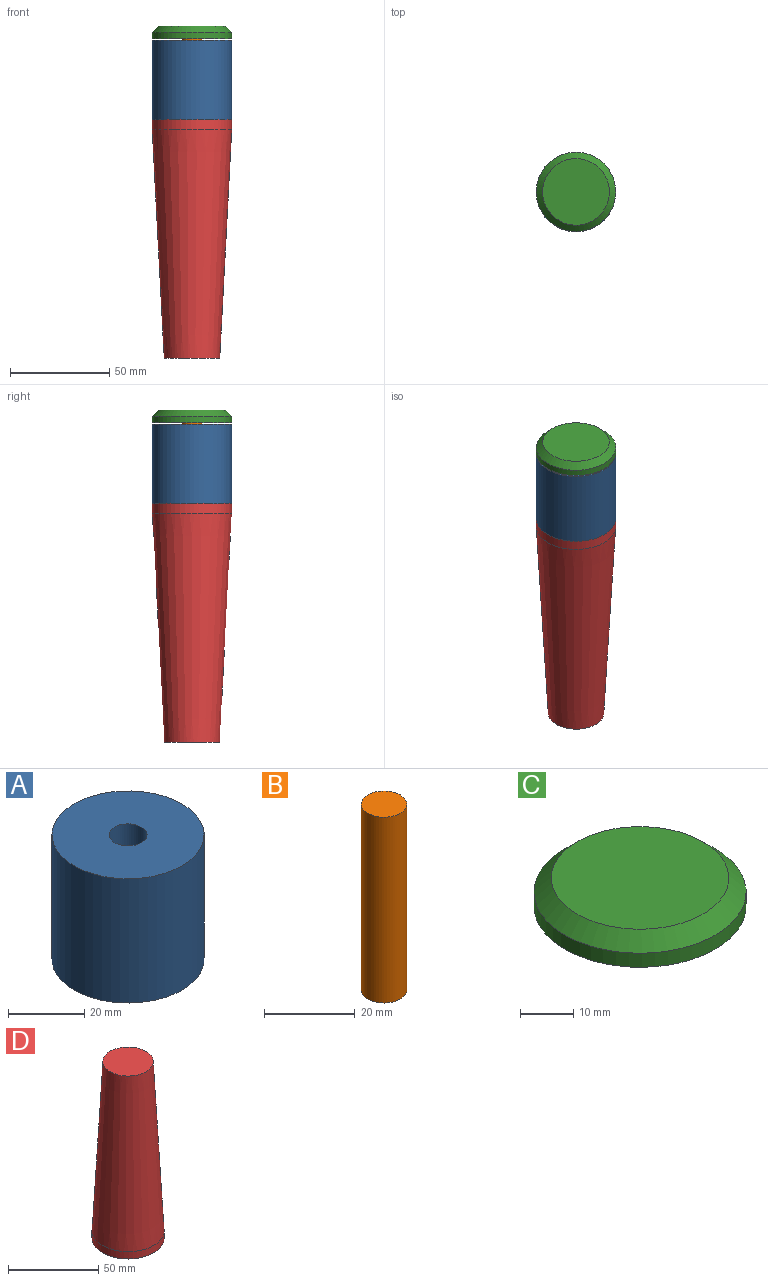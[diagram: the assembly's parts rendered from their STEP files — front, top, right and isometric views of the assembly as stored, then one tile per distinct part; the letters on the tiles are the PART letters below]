
ASSEMBLY  parts=4 mates=3
PART A: 4 faces, bbox 40x40x40 mm
  f0: cylinder r=5mm len=40mm, axis (0,0,-1), area 1256.6mm2, adj f2,f3
  f1: cylinder r=20mm len=40mm, axis (0,0,-1), area 5026.5mm2, adj f2,f3
  f2: plane 40x40mm, normal (0,0,1), area 1178.1mm2, adj f0,f1
  f3: plane 40x40mm, normal (0,0,-1), area 1178.1mm2, adj f0,f1
PART B: 3 faces, bbox 10x10x50 mm
  f0: cylinder r=5mm len=50mm, axis (0,0,-1), area 1570.8mm2, adj f1,f2
  f1: plane 10x10mm, normal (0,0,1), area 78.5mm2, adj f0
  f2: plane 10x10mm, normal (0,0,-1), area 78.5mm2, adj f0
PART C: 4 faces, bbox 40x40x6.5 mm
  f0: cylinder r=20mm len=40mm, axis (0,0,-1), area 408.4mm2, adj f2,f3
  f1: plane 33.5x33.5mm, normal (0,0,1), area 881.4mm2, adj f3
  f2: plane 40x40mm, normal (0,0,-1), area 1256.6mm2, adj f0
  f3: cone r=16.75mm half-angle=45deg, axis (0,0,-1), area 530.6mm2, adj f0,f1
PART D: 6 faces, bbox 40x40x120 mm
  f0: cylinder r=20mm len=40mm, axis (0,0,-1), area 628.3mm2, adj f2,f5
  f1: plane 27.95x27.95mm, normal (0,0,1), area 613.4mm2, adj f5
  f2: plane 40x40mm, normal (0,0,-1), area 1178.1mm2, adj f0,f4
  f3: cone r=0mm half-angle=59deg, axis (0,0,-1), area 91.6mm2, adj f4
  f4: cylinder r=5mm len=10mm, axis (0,0,-1), area 314.2mm2, adj f2,f3
  f5: cone r=13.97mm half-angle=3deg, axis (0,0,-1), area 12290.8mm2, adj f0,f1
PLACE A t=(15.77,311.47,-108.52)mm
PLACE B t=(15.77,311.47,-117.98)mm
PLACE C t=(15.77,311.47,-67.98)mm
PLACE D rot(axis=(-1,0,0),180deg) t=(15.77,311.47,-108.5)mm
MATE slider B.f0 <-> A.f0  axis (0,0,-1) through (15.77,311.47,-117.98)mm
MATE slider B.f0 <-> D.f3  axis (0,0,-1) through (15.77,311.47,-117.98)mm
MATE fastened C.f0 <-> B.f0  axis (0,0,-1) through (15.77,311.47,-67.98)mm
